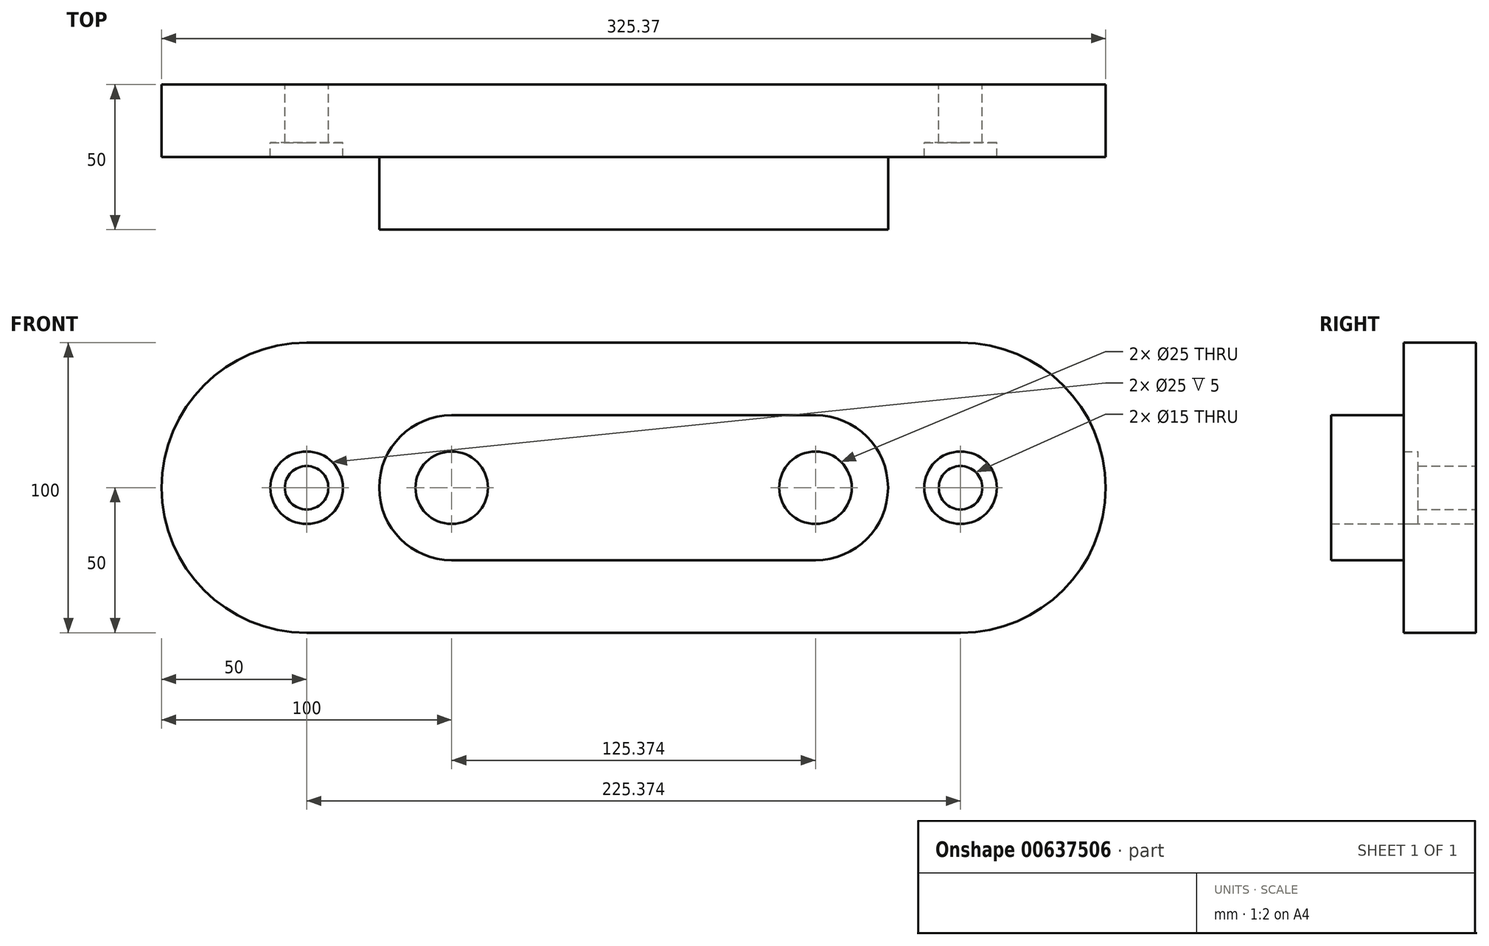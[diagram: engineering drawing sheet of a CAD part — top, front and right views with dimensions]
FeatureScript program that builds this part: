
annotation { "Feature Type Name" : "Feature", "Feature Type Description" : "" }
export const myFeature = defineFeature(function(context is Context, id is Id, definition is map)
    precondition{}
    {
        {
            var Q0;
            Q0=qCreatedBy(makeId("Front.planeOp"),FACE);
            var sketch = newSketch(context, id + "F0", { "sketchPlane" : qUnion([Q0])});
            skArc(sketch, "E0", {"start": v(0, 50) * mm, "mid": v(-50, 0) * mm, "end": v(0, -50) * mm});
            skArc(sketch, "E1", {"start": v(225.37, -50) * mm, "mid": v(275.37, 0) * mm, "end": v(225.37, 50) * mm});
            skLineSegment(sketch, "E2", {"start": v(0, 50) * mm, "end": v(225.37, 50) * mm});
            skLineSegment(sketch, "E3", {"start": v(0, -50) * mm, "end": v(225.37, -50) * mm});
            skArc(sketch, "E4", {"start": v(50, 25) * mm, "mid": v(25, 0) * mm, "end": v(50, -25) * mm});
            skArc(sketch, "E5", {"start": v(175.37, -25) * mm, "mid": v(200.37, 0) * mm, "end": v(175.37, 25) * mm});
            skLineSegment(sketch, "E6", {"start": v(50, 25) * mm, "end": v(175.37, 25) * mm});
            skLineSegment(sketch, "E7", {"start": v(50, -25) * mm, "end": v(175.37, -25) * mm});
            skCircle(sketch, "E8", {"center": v(50, 0) * mm, "radius": 12.5 * mm});
            skCircle(sketch, "E9", {"center": v(175.37, 0) * mm, "radius": 12.5 * mm});
            skCircle(sketch, "E10", {"center": v(0, 0) * mm, "radius": 12.5 * mm});
            skCircle(sketch, "E11", {"center": v(0, 0) * mm, "radius": 7.5 * mm});
            skCircle(sketch, "E12", {"center": v(225.37, 0) * mm, "radius": 12.5 * mm});
            skCircle(sketch, "E13", {"center": v(225.37, 0) * mm, "radius": 7.5 * mm});
            skSolve(sketch);
        }
        {
            var Q0;
            Q0=makeQuery(id+"F0.imprint","IMPRINT",FACE,{"disambiguationData":[TD([[makeQuery(id+"F0.imprint","IMPRINT",EDGE,{"derivedFrom":sQuery(id+"F0.wireOp",EDGE,"E4")}),1.0]])]});
            extrude(context, id + "F1", {"entities" : qUnion([Q0]), "depth" : 50 * mm, "offsetDistance" : 25 * mm});
        }
        {
            var Q0;
            Q0=makeQuery(id+"F0.imprint","IMPRINT",FACE,{"disambiguationData":[TD([[makeQuery(id+"F0.imprint","IMPRINT",EDGE,{"derivedFrom":sQuery(id+"F0.wireOp",EDGE,"E0")}),1.0]])]});
            extrude(context, id + "F2", {"entities" : qUnion([Q0]), "operationType" : NewBodyOperationType.ADD, "depth" : 25 * mm, "offsetDistance" : 25 * mm});
        }
        {
            var Q0;
            Q0=makeQuery(id+"F0.imprint","IMPRINT",FACE,{"disambiguationData":[TD([[makeQuery(id+"F0.imprint","IMPRINT",EDGE,{"derivedFrom":sQuery(id+"F0.wireOp",EDGE,"E10")}),1.0]])]});
            var Q1;
            Q1=makeQuery(id+"F0.imprint","IMPRINT",FACE,{"disambiguationData":[TD([[makeQuery(id+"F0.imprint","IMPRINT",EDGE,{"derivedFrom":sQuery(id+"F0.wireOp",EDGE,"E12")}),1.0]])]});
            extrude(context, id + "F3", {"entities" : qUnion([Q0, Q1]), "operationType" : NewBodyOperationType.ADD, "depth" : 20 * mm, "offsetDistance" : 25 * mm});
        }
    });
